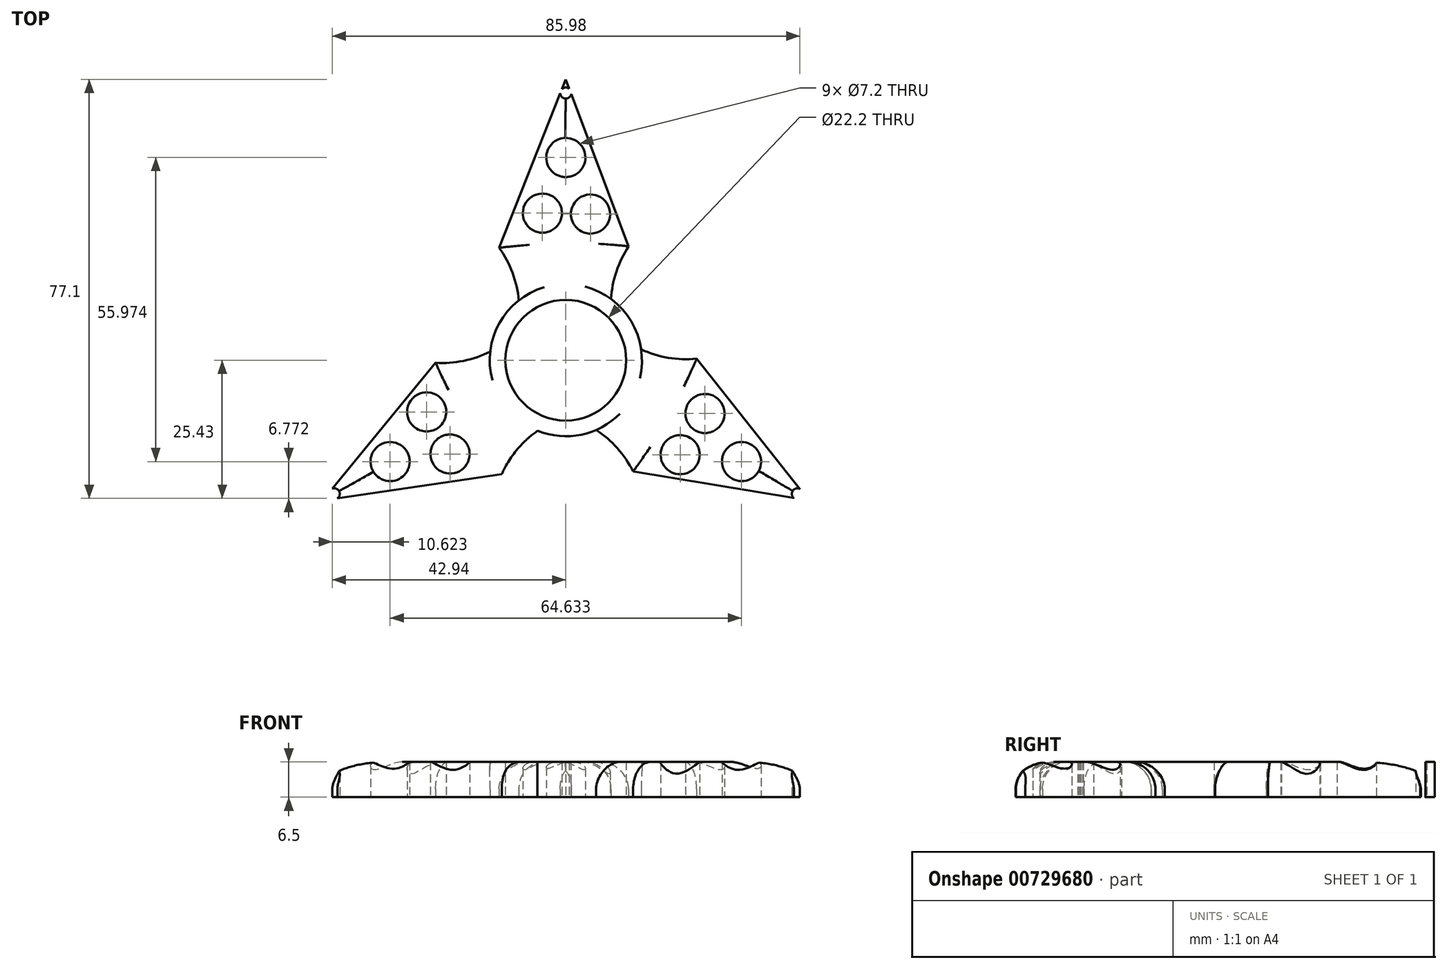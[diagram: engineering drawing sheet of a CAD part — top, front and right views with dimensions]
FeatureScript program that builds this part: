
annotation { "Feature Type Name" : "Feature", "Feature Type Description" : "" }
export const myFeature = defineFeature(function(context is Context, id is Id, definition is map)
    precondition{}
    {
        {
            var Q0;
            Q0=qCreatedBy(makeId("Top.planeOp"),FACE);
            var sketch = newSketch(context, id + "F0", { "sketchPlane" : qUnion([Q0])});
            skCircle(sketch, "E0", {"center": v(0, 0) * mm, "radius": 11.1 * mm});
            skCircle(sketch, "E1", {"center": v(0, 0) * mm, "radius": 14 * mm});
            skArc(sketch, "E2", {"start": v(-11.1, 0) * mm, "mid": v(-8.62, 10.52) * mm, "end": v(-12.28, 20.69) * mm});
            skArc(sketch, "E3", {"start": v(11.55, 20.96) * mm, "mid": v(8.3, 10.55) * mm, "end": v(11.1, 0) * mm});
            skLineSegment(sketch, "E4", {"start": v(-12.28, 20.69) * mm, "end": v(0, 51.67) * mm});
            skLineSegment(sketch, "E5", {"start": v(0, 51.67) * mm, "end": v(11.55, 20.96) * mm});
            skCircle(sketch, "E6", {"center": v(0, 37.32) * mm, "radius": 3.6 * mm});
            skCircle(sketch, "E7", {"center": v(-4.3, 27.07) * mm, "radius": 3.6 * mm});
            skCircle(sketch, "E8", {"center": v(4.55, 26.91) * mm, "radius": 3.6 * mm});
            skCircle(sketch, "E9.1.0", {"center": v(-25.58, -9.52) * mm, "radius": 3.6 * mm});
            skCircle(sketch, "E9.1.1", {"center": v(-21.3, -17.27) * mm, "radius": 3.6 * mm});
            skCircle(sketch, "E9.1.2", {"center": v(-32.32, -18.66) * mm, "radius": 3.6 * mm});
            skLineSegment(sketch, "E9.1.3", {"start": v(-44.75, -25.84) * mm, "end": v(-23.93, -0.48) * mm});
            skLineSegment(sketch, "E9.1.4", {"start": v(-11.77, -20.98) * mm, "end": v(-44.75, -25.84) * mm});
            skArc(sketch, "E9.1.5", {"start": v(5.55, -9.61) * mm, "mid": v(-4.8, -12.73) * mm, "end": v(-11.77, -20.98) * mm});
            skArc(sketch, "E9.1.6", {"start": v(-23.93, -0.48) * mm, "mid": v(-13.28, 1.9) * mm, "end": v(-5.55, 9.61) * mm});
            skCircle(sketch, "E9.2.0", {"center": v(21.03, -17.4) * mm, "radius": 3.6 * mm});
            skCircle(sketch, "E9.2.1", {"center": v(25.6, -9.8) * mm, "radius": 3.6 * mm});
            skCircle(sketch, "E9.2.2", {"center": v(32.32, -18.66) * mm, "radius": 3.6 * mm});
            skLineSegment(sketch, "E9.2.3", {"start": v(44.75, -25.84) * mm, "end": v(12.38, -20.49) * mm});
            skLineSegment(sketch, "E9.2.4", {"start": v(24.06, 0.3) * mm, "end": v(44.75, -25.84) * mm});
            skArc(sketch, "E9.2.5", {"start": v(5.55, 9.61) * mm, "mid": v(13.42, 2.2) * mm, "end": v(24.06, 0.3) * mm});
            skArc(sketch, "E9.2.6", {"start": v(12.38, -20.49) * mm, "mid": v(4.99, -12.46) * mm, "end": v(-5.55, -9.61) * mm});
            skCircle(sketch, "E10", {"center": v(0, 49.18) * mm, "radius": 1.02 * mm});
            skCircle(sketch, "E11.1.0", {"center": v(-42.59, -24.59) * mm, "radius": 1.02 * mm});
            skCircle(sketch, "E11.2.0", {"center": v(42.59, -24.59) * mm, "radius": 1.02 * mm});
            skSolve(sketch);
        }
        {
            var Q0;
            {var subQ0=sQuery(id+"F0.wireOp",EDGE,"E2");var subQ1=sQuery(id+"F0.wireOp",EDGE,"E0");var subQ2=makeQuery(id+"F0.imprint","INTERSECT",VERTEX,{"disambiguationData":[OD(1.0)],"derivedFrom":[subQ1,subQ0]});Q0=makeQuery(id+"F0.imprint","IMPRINT",FACE,{"disambiguationData":[TD([[makeQuery(id+"F0.imprint","IMPRINT",EDGE,{"disambiguationData":[TD([[subQ2,-1.0]])],"derivedFrom":subQ1}),-1.0]])]});}
            var Q1;
            {var subQ0=sQuery(id+"F0.wireOp",EDGE,"E9.2.5");var subQ1=sQuery(id+"F0.wireOp",EDGE,"E0");var subQ2=makeQuery(id+"F0.imprint","INTERSECT",VERTEX,{"disambiguationData":[OD(1.0)],"derivedFrom":[subQ1,subQ0]});Q1=makeQuery(id+"F0.imprint","IMPRINT",FACE,{"disambiguationData":[TD([[makeQuery(id+"F0.imprint","IMPRINT",EDGE,{"disambiguationData":[TD([[subQ2,-1.0]])],"derivedFrom":subQ1}),-1.0]])]});}
            var Q2;
            {var subQ0=sQuery(id+"F0.wireOp",EDGE,"E9.1.5");var subQ1=sQuery(id+"F0.wireOp",EDGE,"E0");var subQ2=makeQuery(id+"F0.imprint","INTERSECT",VERTEX,{"disambiguationData":[OD(1.0)],"derivedFrom":[subQ1,subQ0]});Q2=makeQuery(id+"F0.imprint","IMPRINT",FACE,{"disambiguationData":[TD([[makeQuery(id+"F0.imprint","IMPRINT",EDGE,{"disambiguationData":[TD([[subQ2,-1.0]])],"derivedFrom":subQ1}),-1.0]])]});}
            var Q3;
            {var subQ5=sQuery(id+"F0.wireOp",EDGE,"E0");var subQ8=makeQuery(id+"F0.imprint","INTERSECT",VERTEX,{"disambiguationData":[OD(0.0)],"derivedFrom":[subQ5,sQuery(id+"F0.wireOp",EDGE,"E2")]});Q3=makeQuery(id+"F0.imprint","IMPRINT",FACE,{"disambiguationData":[TD([[makeQuery(id+"F0.imprint","IMPRINT",EDGE,{"disambiguationData":[TD([[subQ8,1.0]])],"derivedFrom":subQ5}),-1.0]])]});}
            var Q4;
            {var subQ0=sQuery(id+"F0.wireOp",EDGE,"E0");var subQ8=makeQuery(id+"F0.imprint","INTERSECT",VERTEX,{"disambiguationData":[OD(0.0)],"derivedFrom":[subQ0,sQuery(id+"F0.wireOp",EDGE,"E9.2.5")]});Q4=makeQuery(id+"F0.imprint","IMPRINT",FACE,{"disambiguationData":[TD([[makeQuery(id+"F0.imprint","IMPRINT",EDGE,{"disambiguationData":[TD([[subQ8,1.0]])],"derivedFrom":subQ0}),-1.0]])]});}
            var Q5;
            {var subQ5=sQuery(id+"F0.wireOp",EDGE,"E0");var subQ6=makeQuery(id+"F0.imprint","INTERSECT",VERTEX,{"disambiguationData":[OD(0.0)],"derivedFrom":[subQ5,sQuery(id+"F0.wireOp",EDGE,"E3")]});Q5=makeQuery(id+"F0.imprint","IMPRINT",FACE,{"disambiguationData":[TD([[makeQuery(id+"F0.imprint","IMPRINT",EDGE,{"disambiguationData":[TD([[subQ6,-1.0]])],"derivedFrom":subQ5}),-1.0]])]});}
            var Q6;
            Q6=makeQuery(id+"F0.imprint","IMPRINT",FACE,{"disambiguationData":[TD([[makeQuery(id+"F0.imprint","IMPRINT",EDGE,{"derivedFrom":sQuery(id+"F0.wireOp",EDGE,"E9.1.0")}),-1.0]])]});
            var Q7;
            Q7=makeQuery(id+"F0.imprint","IMPRINT",FACE,{"disambiguationData":[TD([[makeQuery(id+"F0.imprint","IMPRINT",EDGE,{"derivedFrom":sQuery(id+"F0.wireOp",EDGE,"E9.2.0")}),-1.0]])]});
            var Q8;
            Q8=makeQuery(id+"F0.imprint","IMPRINT",FACE,{"disambiguationData":[TD([[makeQuery(id+"F0.imprint","IMPRINT",EDGE,{"derivedFrom":sQuery(id+"F0.wireOp",EDGE,"E6")}),-1.0]])]});
            var Q9;
            {var subQ0=sQuery(id+"F0.wireOp",EDGE,"E10");var subQ1=sQuery(id+"F0.wireOp",EDGE,"E4");var subQ2=makeQuery(id+"F0.imprint","INTERSECT",VERTEX,{"disambiguationData":[OD(0.0)],"derivedFrom":[subQ1,subQ0]});Q9=makeQuery(id+"F0.imprint","IMPRINT",FACE,{"disambiguationData":[TD([[makeQuery(id+"F0.imprint","IMPRINT",EDGE,{"disambiguationData":[TD([[subQ2,-1.0]])],"derivedFrom":subQ1}),-1.0]])]});}
            var Q10;
            {var subQ0=sQuery(id+"F0.wireOp",EDGE,"E11.2.0");var subQ1=sQuery(id+"F0.wireOp",EDGE,"E9.2.3");var subQ2=makeQuery(id+"F0.imprint","INTERSECT",VERTEX,{"disambiguationData":[OD(0.0)],"derivedFrom":[subQ1,subQ0]});Q10=makeQuery(id+"F0.imprint","IMPRINT",FACE,{"disambiguationData":[TD([[makeQuery(id+"F0.imprint","IMPRINT",EDGE,{"disambiguationData":[TD([[subQ2,-1.0]])],"derivedFrom":subQ1}),-1.0]])]});}
            var Q11;
            {var subQ0=sQuery(id+"F0.wireOp",EDGE,"E11.1.0");var subQ1=sQuery(id+"F0.wireOp",EDGE,"E9.1.3");var subQ2=makeQuery(id+"F0.imprint","INTERSECT",VERTEX,{"disambiguationData":[OD(0.0)],"derivedFrom":[subQ1,subQ0]});Q11=makeQuery(id+"F0.imprint","IMPRINT",FACE,{"disambiguationData":[TD([[makeQuery(id+"F0.imprint","IMPRINT",EDGE,{"disambiguationData":[TD([[subQ2,-1.0]])],"derivedFrom":subQ1}),-1.0]])]});}
            extrude(context, id + "F1", {"entities" : qUnion([Q0, Q1, Q2, Q3, Q4, Q5, Q6, Q7, Q8, Q9, Q10, Q11]), "depth" : 6.5 * mm, "offsetDistance" : 25 * mm});
        }
        {
            var Q0;
            Q0=makeQuery(id+"F1.opExtrude","CAP_EDGE",EDGE,{"disambiguationData":[OSD([sQuery(id+"F0.wireOp",EDGE,"E9.1.4")])],"isStart":false});
            var Q1;
            Q1=makeQuery(id+"F1.opExtrude","CAP_EDGE",EDGE,{"disambiguationData":[OSD([sQuery(id+"F0.wireOp",EDGE,"E9.1.3")])],"isStart":false});
            var Q2;
            Q2=makeQuery(id+"F1.opExtrude","CAP_EDGE",EDGE,{"disambiguationData":[OSD([sQuery(id+"F0.wireOp",EDGE,"E9.1.6")])],"isStart":false});
            var Q3;
            Q3=makeQuery(id+"F1.opExtrude","CAP_EDGE",EDGE,{"disambiguationData":[OSD([sQuery(id+"F0.wireOp",EDGE,"E2")])],"isStart":false});
            var Q4;
            Q4=makeQuery(id+"F1.opExtrude","CAP_EDGE",EDGE,{"disambiguationData":[OSD([sQuery(id+"F0.wireOp",EDGE,"E4")])],"isStart":false});
            var Q5;
            Q5=makeQuery(id+"F1.opExtrude","CAP_EDGE",EDGE,{"disambiguationData":[OSD([sQuery(id+"F0.wireOp",EDGE,"E5")])],"isStart":false});
            var Q6;
            Q6=makeQuery(id+"F1.opExtrude","CAP_EDGE",EDGE,{"disambiguationData":[OSD([sQuery(id+"F0.wireOp",EDGE,"E3")])],"isStart":false});
            var Q7;
            Q7=makeQuery(id+"F1.opExtrude","CAP_EDGE",EDGE,{"disambiguationData":[OSD([sQuery(id+"F0.wireOp",EDGE,"E9.2.5")])],"isStart":false});
            var Q8;
            Q8=makeQuery(id+"F1.opExtrude","CAP_EDGE",EDGE,{"disambiguationData":[OSD([sQuery(id+"F0.wireOp",EDGE,"E9.2.4")])],"isStart":false});
            var Q9;
            Q9=makeQuery(id+"F1.opExtrude","CAP_EDGE",EDGE,{"disambiguationData":[OSD([sQuery(id+"F0.wireOp",EDGE,"E9.2.3")])],"isStart":false});
            var Q10;
            Q10=makeQuery(id+"F1.opExtrude","CAP_EDGE",EDGE,{"disambiguationData":[OSD([sQuery(id+"F0.wireOp",EDGE,"E9.2.6")])],"isStart":false});
            fillet(context, id + "F2", {"entities" : qUnion([Q0, Q1, Q2, Q3, Q4, Q5, Q6, Q7, Q8, Q9, Q10]), "radius" : 5 * mm, "tangentPropagation" : true, "allowEdgeOverflow" : false});
        }
    });
